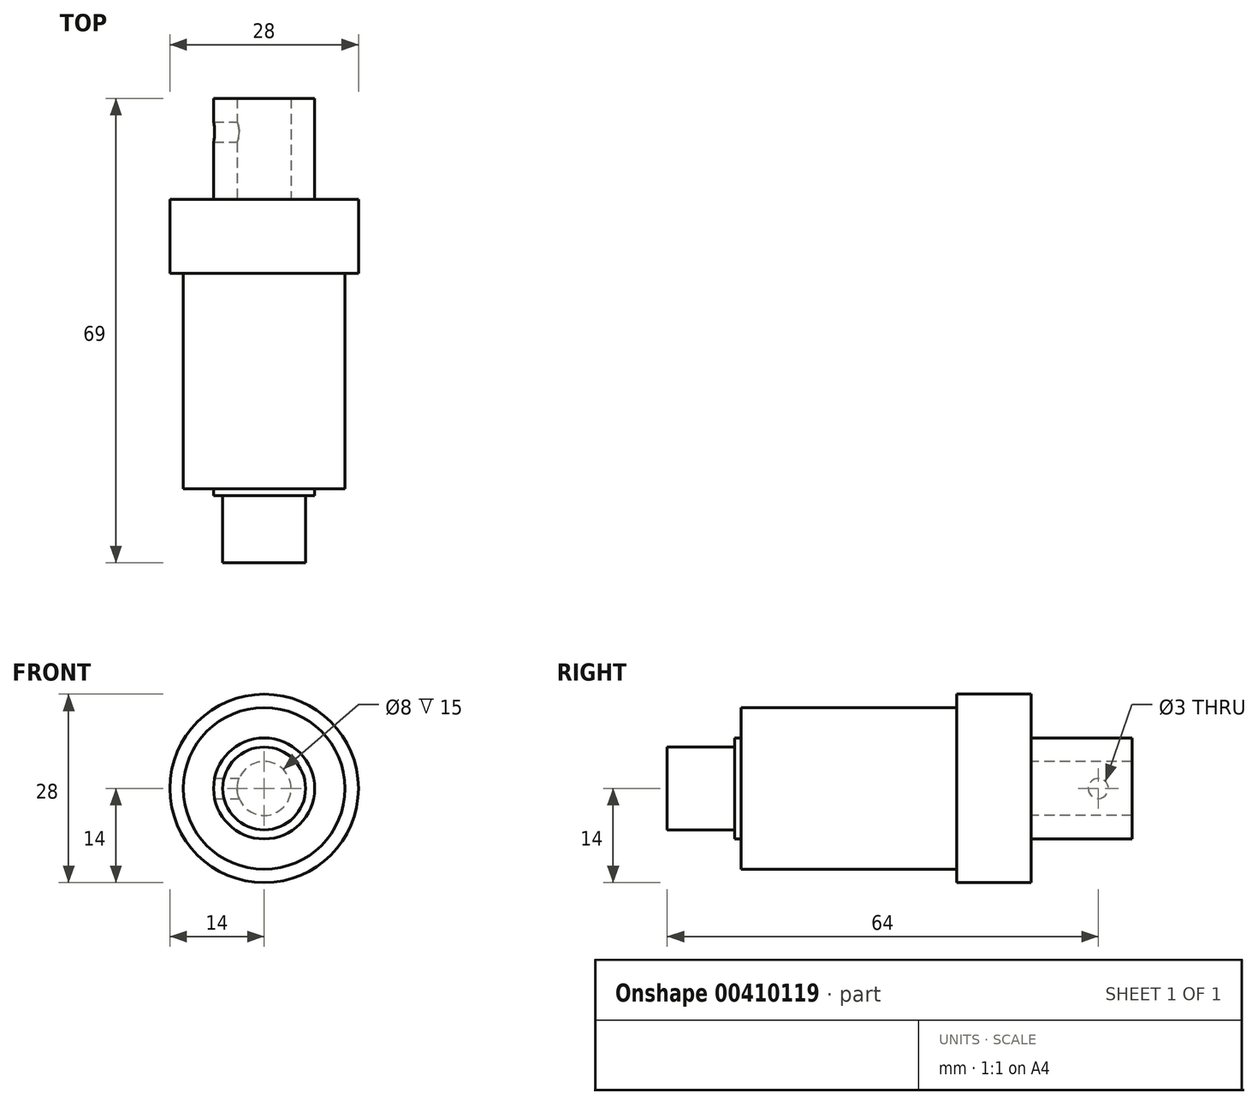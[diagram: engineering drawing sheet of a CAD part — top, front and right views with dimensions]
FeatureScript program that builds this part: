
annotation { "Feature Type Name" : "Feature", "Feature Type Description" : "" }
export const myFeature = defineFeature(function(context is Context, id is Id, definition is map)
    precondition{}
    {
        {
            var Q0;
            Q0=qCreatedBy(makeId("Front.planeOp"),FACE);
            var sketch = newSketch(context, id + "F0", { "sketchPlane" : qUnion([Q0])});
            skCircle(sketch, "E0", {"center": v(0, 0) * mm, "radius": 14 * mm});
            skSolve(sketch);
        }
        {
            var Q0;
            Q0 = qSketchRegion(id + "F0", true);
            extrude(context, id + "F1", {"entities" : qUnion([Q0]), "depth" : 11 * mm});
        }
        {
            var Q0;
            Q0=makeQuery(id+"F1.opExtrude","CAP_FACE",FACE,{"disambiguationData":[OSD([sQuery(id+"F0.wireOp",EDGE,"E0")])],"isStart":false});
            var sketch = newSketch(context, id + "F2", { "sketchPlane" : qUnion([Q0])});
            skCircle(sketch, "E1", {"center": v(0, 0) * mm, "radius": 12 * mm});
            skSolve(sketch);
        }
        {
            var Q0;
            Q0 = qSketchRegion(id + "F2", true);
            extrude(context, id + "F3", {"entities" : qUnion([Q0]), "operationType" : NewBodyOperationType.ADD, "depth" : 32 * mm});
        }
        {
            var Q0;
            Q0=makeQuery(id+"F1.opExtrude","CAP_FACE",FACE,{"disambiguationData":[OSD([sQuery(id+"F0.wireOp",EDGE,"E0")])],"isStart":true});
            var sketch = newSketch(context, id + "F4", { "sketchPlane" : qUnion([Q0])});
            skCircle(sketch, "E2", {"center": v(0, 0) * mm, "radius": 4 * mm});
            skCircle(sketch, "E3", {"center": v(0, 0) * mm, "radius": 7.5 * mm});
            skSolve(sketch);
        }
        {
            var Q0;
            Q0 = qSketchRegion(id + "F4", true);
            extrude(context, id + "F5", {"entities" : qUnion([Q0]), "operationType" : NewBodyOperationType.ADD, "depth" : 15 * mm});
        }
        {
            var Q0;
            Q0=makeQuery(id+"F3.opExtrude","CAP_FACE",FACE,{"disambiguationData":[OSD([sQuery(id+"F2.wireOp",EDGE,"E1")])],"isStart":false});
            var sketch = newSketch(context, id + "F6", { "sketchPlane" : qUnion([Q0])});
            skCircle(sketch, "E4", {"center": v(0, 0) * mm, "radius": 7.5 * mm});
            skSolve(sketch);
        }
        {
            var Q0;
            Q0 = qSketchRegion(id + "F6", true);
            extrude(context, id + "F7", {"entities" : qUnion([Q0]), "operationType" : NewBodyOperationType.ADD, "depth" : 1 * mm});
        }
        {
            var Q0;
            Q0=makeQuery(id+"F7.opExtrude","CAP_FACE",FACE,{"disambiguationData":[OSD([sQuery(id+"F6.wireOp",EDGE,"E4")])],"isStart":false});
            var sketch = newSketch(context, id + "F8", { "sketchPlane" : qUnion([Q0])});
            skCircle(sketch, "E5", {"center": v(0, 0) * mm, "radius": 6.15 * mm});
            skSolve(sketch);
        }
        {
            var Q0;
            Q0 = qSketchRegion(id + "F8", true);
            extrude(context, id + "F9", {"entities" : qUnion([Q0]), "operationType" : NewBodyOperationType.ADD, "depth" : 10 * mm});
        }
        {
            var Q0;
            Q0=qCreatedBy(makeId("Right.planeOp"),FACE);
            var sketch = newSketch(context, id + "F10", { "sketchPlane" : qUnion([Q0])});
            skCircle(sketch, "E6", {"center": v(10, 0) * mm, "radius": 1.5 * mm});
            skSolve(sketch);
        }
        {
            var Q0;
            Q0 = qSketchRegion(id + "F10", true);
            extrude(context, id + "F11", {"entities" : qUnion([Q0]), "operationType" : NewBodyOperationType.REMOVE, "oppositeDirection" : true, "depth" : 25 * mm});
        }
    });
